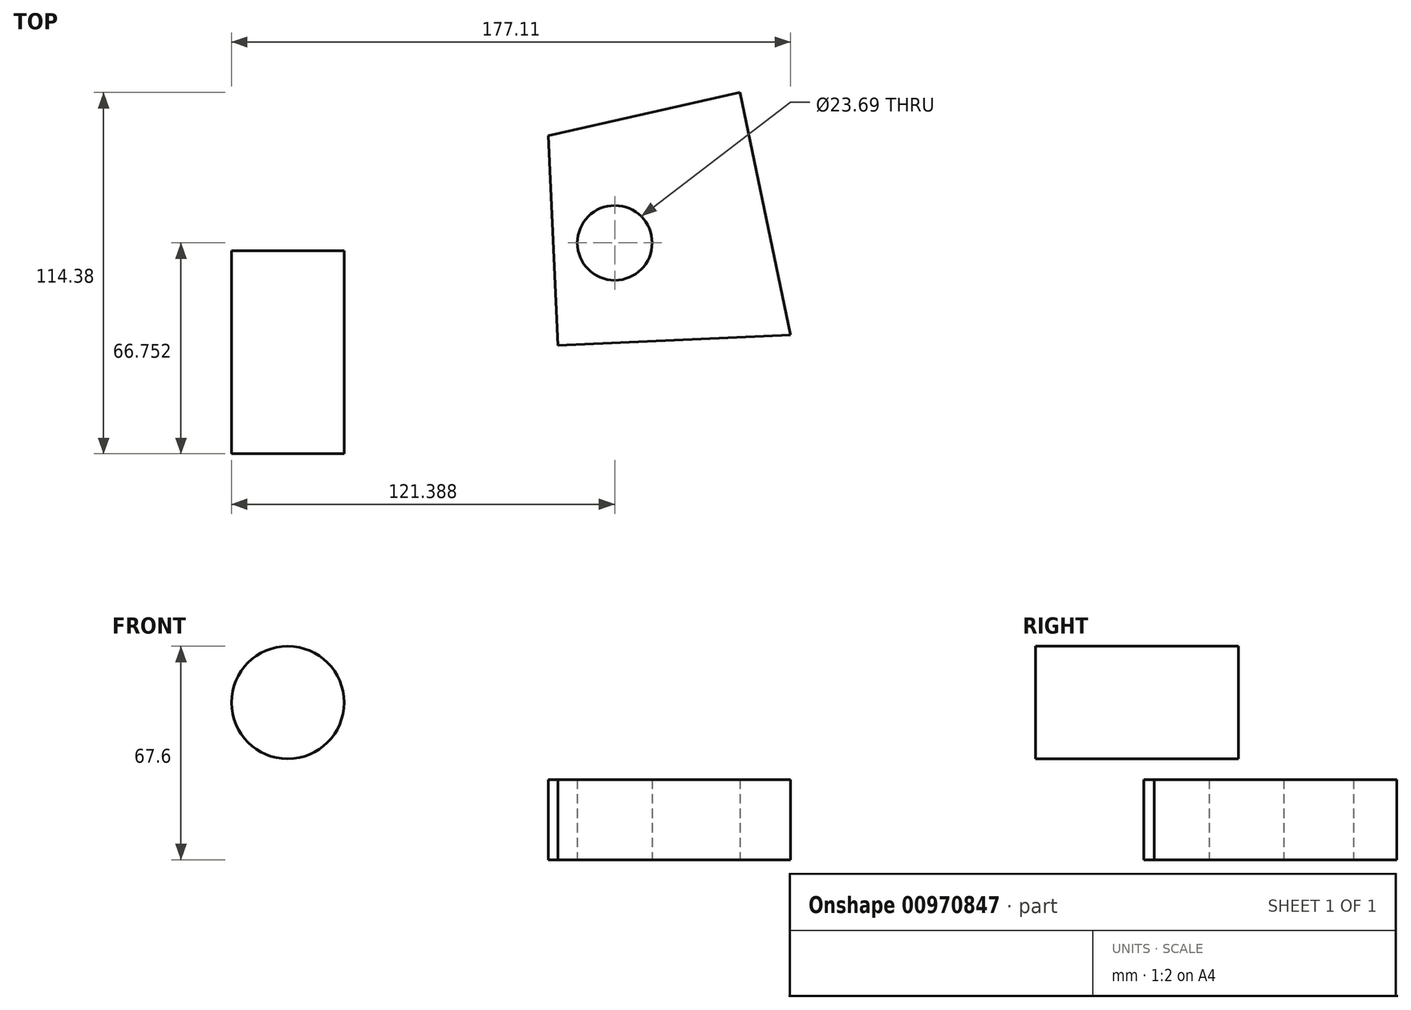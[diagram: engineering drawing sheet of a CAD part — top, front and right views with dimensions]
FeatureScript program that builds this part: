
annotation { "Feature Type Name" : "Feature", "Feature Type Description" : "" }
export const myFeature = defineFeature(function(context is Context, id is Id, definition is map)
    precondition{}
    {
        {
            var Q0;
            Q0=qCreatedBy(makeId("Top.planeOp"),FACE);
            var sketch = newSketch(context, id + "F0", { "sketchPlane" : qUnion([Q0])});
            skLineSegment(sketch, "E0", {"start": v(-47.07, 36.4) * mm, "end": v(-44.03, -30) * mm});
            skLineSegment(sketch, "E1", {"start": v(-44.03, -30) * mm, "end": v(29.69, -26.63) * mm});
            skLineSegment(sketch, "E2", {"start": v(29.69, -26.63) * mm, "end": v(13.64, 50.12) * mm});
            skLineSegment(sketch, "E3", {"start": v(13.64, 50.12) * mm, "end": v(-47.07, 36.4) * mm});
            skLineSegment(sketch, "E4", {"start": v(29.69, -26.63) * mm, "end": v(29.69, -26.63) * mm});
            skCircle(sketch, "E5", {"center": v(-26.03, 2.5) * mm, "radius": 11.84 * mm});
            skSolve(sketch);
        }
        {
            var Q0;
            Q0 = qSketchRegion(id + "F0", true);
            extrude(context, id + "F1", {"entities" : qUnion([Q0]), "depth" : 25.4 * mm, "offsetDistance" : 25.4 * mm});
        }
        {
            var Q0;
            Q0=qCreatedBy(makeId("Front.planeOp"),FACE);
            var sketch = newSketch(context, id + "F2", { "sketchPlane" : qUnion([Q0])});
            skCircle(sketch, "E6", {"center": v(-129.6, 49.78) * mm, "radius": 17.82 * mm});
            skSolve(sketch);
        }
        {
            var Q0;
            Q0 = qSketchRegion(id + "F2", true);
            extrude(context, id + "F3", {"entities" : qUnion([Q0]), "depth" : 64.26 * mm, "offsetDistance" : 25.4 * mm});
        }
    });
